# Revit family: Domotics-DomesticRanges-GEWISS-CHORUS_SIGNALLING-RINGER_BUZZER
name_source: partatom
category: Apparecchi elettrici
revit_build: Autodesk Revit 2016 (Build: 20161004_0715(x64)
units: mm (PartAtom-declared; Revit-internal decimal feet)

## family parameters
Condiviso = Sì
Host = Superficie
Mantenere orientamento annotazione = Sì
Punto di calcolo locali = Sì
Quota connettore circolare = Usa diametro
Taglio con vuoti quando caricato = Sì
Tipo di parte = Normale

## types (18) — shared parameters
1M = No
2M = Sì
Catalogue = DOMOTICS
Catalogue Range = CHORUS - DOMESTIC RANGE
Electrocod = 0132
IDF = a0c2cdf7-cc94-41eb-b049-a8570d956207
IDT = 523baa4e-081c-4c4c-8f65-c97c42e469a2
Immagine tipo = GW14612.jpg
Produttore = GEWISS S.p.A.
Prospetto di default = 1219 mm
Technical sheet = https://www.gewiss.com
URL = https://www.gewiss.com
Version file RFA = 19.0
finitura = Titanio
larghezza = 32 mm  [stored 0.104987 ft]

## per-type parameters (varying)
| type | Colour | Description. | Descrizione | EAN code | Max power consumption | Modello | No. Chorus modules | No. Chorus modules: | Power input | SEO | Sound intensity | Supply voltage | Type | Type: |
| GW14606 - Buzzer, 12Vac-50hz 8VA 1M titanium | Titanium | Buzzer | BUZZER, 12VAC-50Hz 8VA 1M TITANIUM | 8011564268289 | 8VA | GW14606 | 1 | 1 | 8VA | Buzzer | 70 dB (at 1 m) | 12V ac - 50 Hz |  |  |
| GW12606 - Buzzer 12Vac-50hz 8VA 1M black | Black | Buzzer | BUZZER 12VAC-50Hz 8VA 1M BLACK | 8011564269217 | 8VA | GW12606 | 1 | 1 | 8VA | Buzzer | 70 dB (at 1 m) | 12V ac - 50 Hz |  |  |
| GW10607 - Buzzer, 230V-50hz 8VA 1M white | White | Buzzer | BUZZER, 230VAC-50Hz 8VA 1M WHITE | 8011564259461 | 8VA | GW10607 | 1 | 1 | 8VA | Buzzer | 70 dB (at 1 m) | 230V ac - 50 Hz |  |  |
| GW14601 - Ringer, 12Vac-50hz 8VA 1M titanium | Titanium | Bell | RINGER, 12VAC-50Hz 8VA 1M TITANIUM | 8011564268203 | 8VA | GW14601 | 1 | 1 | 8VA | Ringer | 80 dB (at 1 m) | 12V ac - 50 Hz |  |  |
| GW10611 - Ringer, 3 ind inputs 12V ac/dc 2M white | White | Ringer (3 inputs) | RINGER, 3 IND INPUTS 12V AC/DC 2M WHITE | 8011564260894 | 3VA | GW10611 | 2 | 2 | 3VA | Ringer | 80 dB (at 1 m) | 12V ac/dc | 3 shades | 3 shades |
| GW10602 - Ringer, 230V-50hz 8VA 1M white | White | Bell | RINGER, 230VAC-50Hz 8VA 1M WHITE | 8011564259485 | 8VA | GW10602 | 1 | 1 | 8VA | Ringer | 80 dB (at 1 m) | 230V ac - 50 Hz |  |  |
| GW12601 - Ringer 12Vac-50hz 8VA 1M black | Black | Bell | RINGER 12VAC-50Hz 8VA 1M BLACK | 8011564269194 | 8VA | GW12601 | 1 | 1 | 8VA | Ringer | 80 dB (at 1 m) | 12V ac - 50 Hz |  |  |
| GW10606 - Buzzer, 12Vac-50hz 8VA 1M white | White | Buzzer | BUZZER, 12VAC-50Hz 8VA 1M WHITE | 8011564259478 | 8VA | GW10606 | 1 | 1 | 8VA | Buzzer | 70 dB (at 1 m) | 12V ac - 50 Hz |  |  |
| GW12612 - Ringer 3 ind inputs 230V-50hz 2M black | Black | Ringer (3 inputs) | RINGER 3 IND INPUTS 230VAC-50Hz 2M BLACK | 8011564267954 | 6VA | GW12612 | 2 | 2 | 6VA | Ringer | 80 dB (at 1 m) | 230V ac - 50 Hz | 3 shades | 3 shades |
| GW10601 - Ringer, 12Vac-50hz 8VA 1M white | White | Bell | RINGER, 12VAC-50Hz 8VA 1M WHITE | 8011564259492 | 8VA | GW10601 | 1 | 1 | 8VA | Ringer | 80 dB (at 1 m) | 12V ac - 50 Hz |  |  |
| GW14611 - Ringer, 3 ind inputs 12V ac/dc 2M titanium | Titanium | Ringer (3 inputs) | RINGER, 3 IND INPUTS 12V AC/DC 2M T | 8011564268340 | 3VA | GW14611 | 2 | 2 | 3VA | Ringer | 80 dB (at 1 m) | 12V ac/dc | 3 shades | 3 shades |
| GW12611 - Ringer 3 ind inputs 12V ac/dc 2M black | Black | Ringer (3 inputs) | RINGER 3 IND INPUTS 12V AC/DC 2M BLACK | 8011564267947 | 3VA | GW12611 | 2 | 2 | 3VA | Ringer | 80 dB (at 1 m) | 12V ac/dc | 3 shades | 3 shades |
| GW14607 - Buzzer, 230V-50hz 8VA 1M titanium | Titanium | Buzzer | BUZZER, 230VAC-50Hz 8VA 1M TITANIUM | 8011564268319 | 8VA | GW14607 | 1 | 1 | 8VA | Buzzer | 70 dB (at 1 m) | 230V ac - 50 Hz |  |  |
| GW14602 - Ringer, 230V-50hz 8VA 1M titanium | Titanium | Bell | RINGER, 230VAC-50Hz 8VA 1M TITANIUM | 8011564268258 | 8VA | GW14602 | 1 | 1 | 8VA | Ringer | 80 dB (at 1 m) | 230V ac - 50 Hz |  |  |
| GW12607 - Buzzer 230V-50hz 8VA 1M black | Black | Buzzer | BUZZER 230VAC-50Hz 8VA 1M BLACK | 8011564269224 | 8VA | GW12607 | 1 | 1 | 8VA | Buzzer | 70 dB (at 1 m) | 230V ac - 50 Hz |  |  |
| GW12602 - Ringer 230V-50hz 8VA 1M black | Black | Bell | RINGER 230VAC-50Hz 8VA 1M BLACK | 8011564269200 | 8VA | GW12602 | 1 | 1 | 8VA | Ringer | 80 dB (at 1 m) | 230V ac - 50 Hz |  |  |
| GW10612 - Ringer 3 ind inputs 230V-50hz 2M white | White | Ringer (3 inputs) | RINGER 3 IND INPUTS 230VAC-50Hz 2M WHITE | 8011564260900 | 6VA | GW10612 | 2 | 2 | 6VA | Ringer | 80 dB (at 1 m) | 230V ac - 50 Hz | 3 shades | 3 shades |
| GW14612 - Ringer, 3 ind inputs 230V-50hz 2M titanium | Titanium | Ringer (3 inputs) | RINGER, 3 IND INPUTS 230VAC-50Hz 2M T | 8011564268371 | 6VA | GW14612 | 2 | 2 | 6VA | Ringer | 80 dB (at 1 m) | 230V ac - 50 Hz | 3 shades | 3 shades |

note: [stored X ft] marks values corroborated as IEEE doubles in the binary element streams (Revit-internal decimal feet)

## geometry (parser evidence)
native form markers: Sweep x2
no freeform markers — native parametric forms only
